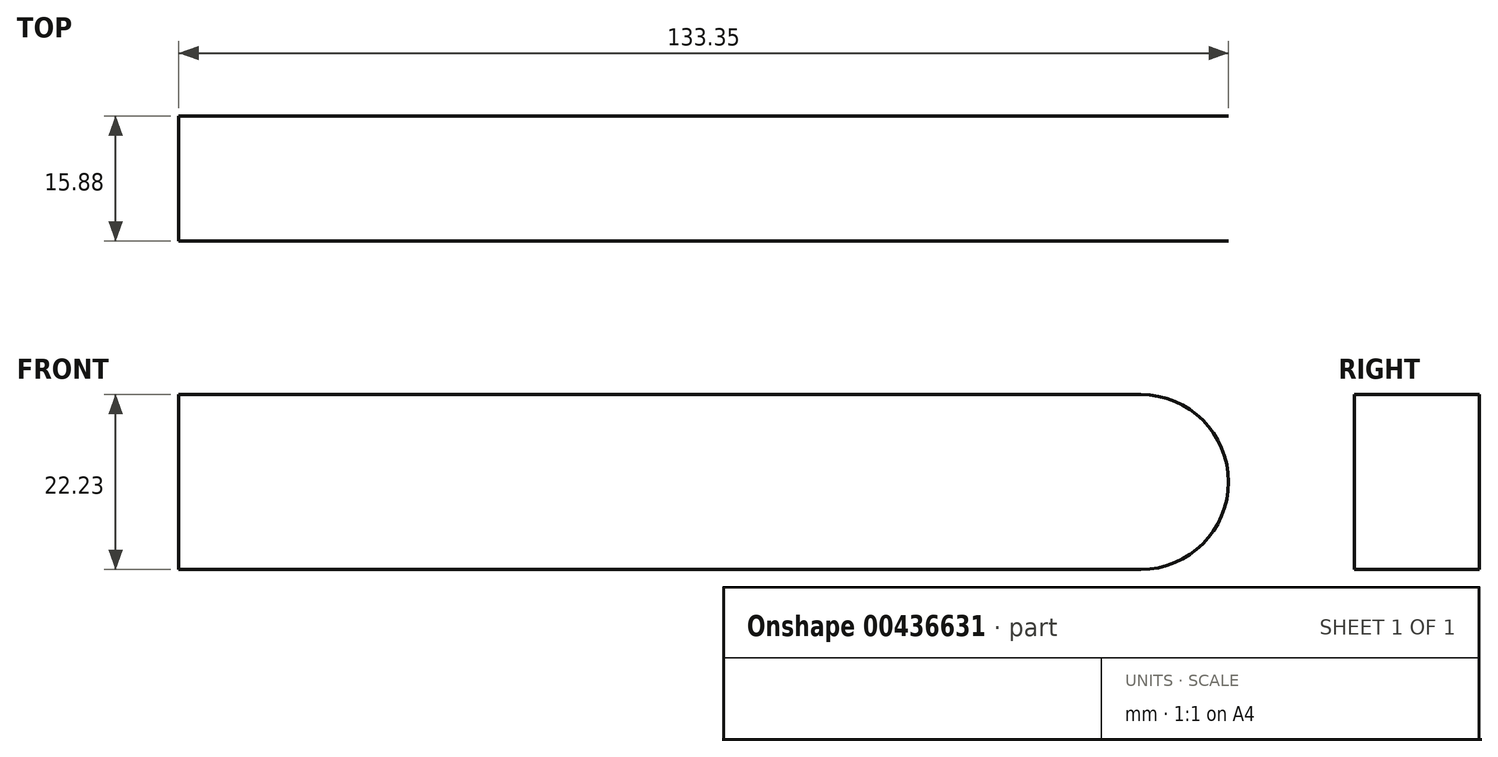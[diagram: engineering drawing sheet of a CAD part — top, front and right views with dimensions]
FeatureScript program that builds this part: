
annotation { "Feature Type Name" : "Feature", "Feature Type Description" : "" }
export const myFeature = defineFeature(function(context is Context, id is Id, definition is map)
    precondition{}
    {
        {
            var Q0;
            Q0=qCreatedBy(makeId("Front.planeOp"),FACE);
            var sketch = newSketch(context, id + "F0", { "sketchPlane" : qUnion([Q0])});
            skLineSegment(sketch, "E0.bottom", {"start": v(-73.66, 9.59) * mm, "end": v(48.56, 9.59) * mm});
            skLineSegment(sketch, "E0.top", {"start": v(-73.66, -12.64) * mm, "end": v(48.56, -12.64) * mm});
            skLineSegment(sketch, "E0.left", {"start": v(-73.66, 9.59) * mm, "end": v(-73.66, -12.64) * mm});
            skLineSegment(sketch, "E0.right", {"start": v(59.69, -1.51) * mm, "end": v(59.69, -1.54) * mm});
            skPoint(sketch, "E1.visualSharp", {"position": v(59.69, 9.59) * mm});
            skArc(sketch, "E1.filletArc", {"start": v(59.69, -1.54) * mm, "mid": v(56.43, 6.33) * mm, "end": v(48.56, 9.59) * mm});
            skPoint(sketch, "E2.visualSharp", {"position": v(59.69, -12.64) * mm});
            skArc(sketch, "E2.filletArc", {"start": v(48.56, -12.64) * mm, "mid": v(56.43, -9.38) * mm, "end": v(59.69, -1.51) * mm});
            skSolve(sketch);
        }
        {
            var Q0;
            {var subQ1=sQuery(id+"F0.wireOp",EDGE,"E0.bottom");Q0=makeQuery(id+"F0.imprint","IMPRINT",FACE,{"disambiguationData":[TD([[makeQuery(id+"F0.imprint","IMPRINT",EDGE,{"derivedFrom":subQ1}),-1.0]])]});}
            extrude(context, id + "F1", {"entities" : qUnion([Q0]), "depth" : 15.88 * mm, "offsetDistance" : 25.4 * mm});
        }
    });
